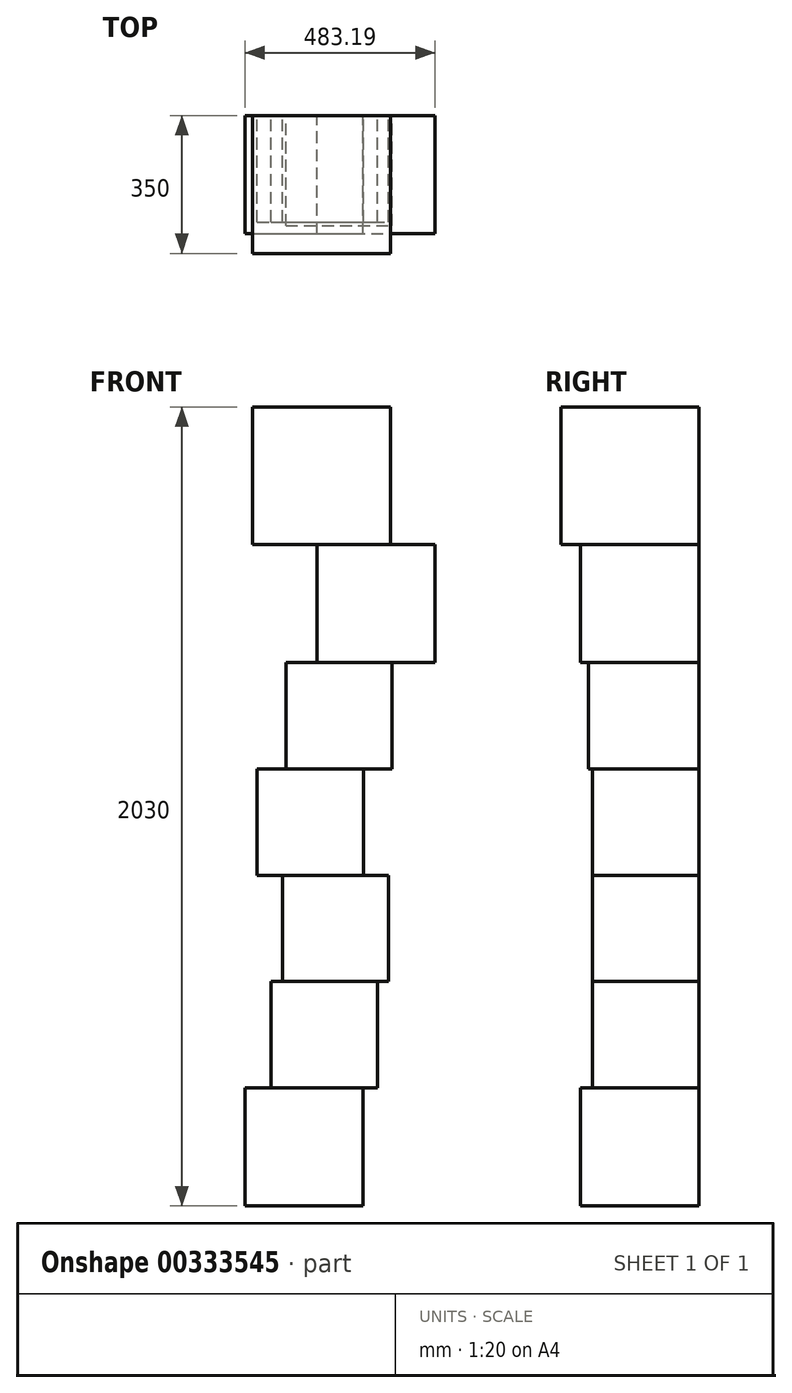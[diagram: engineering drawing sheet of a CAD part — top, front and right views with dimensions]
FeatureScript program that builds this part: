
annotation { "Feature Type Name" : "Feature", "Feature Type Description" : "" }
export const myFeature = defineFeature(function(context is Context, id is Id, definition is map)
    precondition{}
    {
        {
            assignVariable(context, id + "F0", {"name" : "a", "anyValue" : 270});
        }
        {
            assignVariable(context, id + "F1", {"name" : "b", "anyValue" : 350});
        }
        {
            assignVariable(context, id + "F2", {"name" : "c", "anyValue" : 300});
        }
        {
            var Q0;
            Q0=qCreatedBy(makeId("Front.planeOp"),FACE);
            var sketch = newSketch(context, id + "F3", { "sketchPlane" : qUnion([Q0])});
            skLineSegment(sketch, "E0.bottom", {"start": v(0, 0) * mm, "end": v(500, 0) * mm});
            skLineSegment(sketch, "E0.top", {"start": v(0, 60) * mm, "end": v(500, 60) * mm});
            skLineSegment(sketch, "E0.left", {"start": v(0, 0) * mm, "end": v(0, 60) * mm});
            skLineSegment(sketch, "E0.right", {"start": v(500, 0) * mm, "end": v(500, 60) * mm});
            skLineSegment(sketch, "E1", {"start": v(0, 0) * mm, "end": v(500, 0) * mm, "construction": true});
            skLineSegment(sketch, "E2", {"start": v(0, 0) * mm, "end": v(0, 60) * mm, "construction": true});
            skLineSegment(sketch, "E3.bottom", {"start": v(13.65, 60) * mm, "end": v(363.65, 60) * mm});
            skLineSegment(sketch, "E3.top", {"start": v(13.65, 410) * mm, "end": v(363.65, 410) * mm});
            skLineSegment(sketch, "E3.left", {"start": v(13.65, 60) * mm, "end": v(13.65, 410) * mm});
            skLineSegment(sketch, "E3.right", {"start": v(363.65, 60) * mm, "end": v(363.65, 410) * mm});
            skLineSegment(sketch, "E4.bottom", {"start": v(106.14, 410) * mm, "end": v(406.14, 410) * mm});
            skLineSegment(sketch, "E4.top", {"start": v(106.14, 710) * mm, "end": v(406.14, 710) * mm});
            skLineSegment(sketch, "E4.left", {"start": v(106.14, 410) * mm, "end": v(106.14, 710) * mm});
            skLineSegment(sketch, "E4.right", {"start": v(406.14, 410) * mm, "end": v(406.14, 710) * mm});
            skLineSegment(sketch, "E5.bottom", {"start": v(172.85, 710) * mm, "end": v(442.85, 710) * mm});
            skLineSegment(sketch, "E5.top", {"start": v(172.85, 980) * mm, "end": v(442.85, 980) * mm});
            skLineSegment(sketch, "E5.left", {"start": v(172.85, 710) * mm, "end": v(172.85, 980) * mm});
            skLineSegment(sketch, "E5.right", {"start": v(442.85, 710) * mm, "end": v(442.85, 980) * mm});
            skLineSegment(sketch, "E6.bottom", {"start": v(201.48, 980) * mm, "end": v(471.48, 980) * mm});
            skLineSegment(sketch, "E6.top", {"start": v(201.48, 1250) * mm, "end": v(471.48, 1250) * mm});
            skLineSegment(sketch, "E6.left", {"start": v(201.48, 980) * mm, "end": v(201.48, 1250) * mm});
            skLineSegment(sketch, "E6.right", {"start": v(471.48, 980) * mm, "end": v(471.48, 1250) * mm});
            skLineSegment(sketch, "E7.bottom", {"start": v(0, 0) * mm, "end": v(900, 0) * mm, "construction": true});
            skLineSegment(sketch, "E7.top", {"start": v(0, 1750) * mm, "end": v(900, 1750) * mm, "construction": true});
            skLineSegment(sketch, "E7.left", {"start": v(0, 0) * mm, "end": v(0, 1750) * mm, "construction": true});
            skLineSegment(sketch, "E7.right", {"start": v(900, 0) * mm, "end": v(900, 1750) * mm, "construction": true});
            skLineSegment(sketch, "E8", {"start": v(0, 900) * mm, "end": v(900, 900) * mm, "construction": true});
            skLineSegment(sketch, "E9.bottom", {"start": v(137.05, 1250) * mm, "end": v(407.05, 1250) * mm});
            skLineSegment(sketch, "E9.top", {"start": v(137.05, 1520) * mm, "end": v(407.05, 1520) * mm});
            skLineSegment(sketch, "E9.left", {"start": v(137.05, 1250) * mm, "end": v(137.05, 1520) * mm});
            skLineSegment(sketch, "E9.right", {"start": v(407.05, 1250) * mm, "end": v(407.05, 1520) * mm});
            skLineSegment(sketch, "E10.bottom", {"start": v(210.21, 1520) * mm, "end": v(480.21, 1520) * mm});
            skLineSegment(sketch, "E10.top", {"start": v(210.21, 1790) * mm, "end": v(480.21, 1790) * mm});
            skLineSegment(sketch, "E10.left", {"start": v(210.21, 1520) * mm, "end": v(210.21, 1790) * mm});
            skLineSegment(sketch, "E10.right", {"start": v(480.21, 1520) * mm, "end": v(480.21, 1790) * mm});
            skLineSegment(sketch, "E11", {"start": v(0, 1750) * mm, "end": v(0, 2550) * mm, "construction": true});
            skLineSegment(sketch, "E12", {"start": v(0, 2550) * mm, "end": v(900, 2550) * mm, "construction": true});
            skLineSegment(sketch, "E13", {"start": v(900, 1750) * mm, "end": v(900, 2550) * mm, "construction": true});
            skLineSegment(sketch, "E14.bottom", {"start": v(289.33, 1790) * mm, "end": v(589.33, 1790) * mm});
            skLineSegment(sketch, "E14.top", {"start": v(289.33, 2090) * mm, "end": v(589.33, 2090) * mm});
            skLineSegment(sketch, "E14.left", {"start": v(289.33, 1790) * mm, "end": v(289.33, 2090) * mm});
            skLineSegment(sketch, "E14.right", {"start": v(589.33, 1790) * mm, "end": v(589.33, 2090) * mm});
            skLineSegment(sketch, "E15.bottom", {"start": v(475.94, 2090) * mm, "end": v(125.94, 2090) * mm});
            skLineSegment(sketch, "E15.top", {"start": v(475.94, 2440) * mm, "end": v(125.94, 2440) * mm});
            skLineSegment(sketch, "E15.left", {"start": v(475.94, 2090) * mm, "end": v(475.94, 2440) * mm});
            skLineSegment(sketch, "E15.right", {"start": v(125.94, 2090) * mm, "end": v(125.94, 2440) * mm});
            skSolve(sketch);
        }
        {
            var Q0;
            Q0=makeQuery(id+"F3.imprint","IMPRINT",FACE,{"disambiguationData":[TD([[makeQuery(id+"F3.imprint","IMPRINT",EDGE,{"derivedFrom":sQuery(id+"F3.wireOp",EDGE,"E3.bottom")}),1.0]])]});
            var Q1;
            Q1=makeQuery(id+"F3.imprint","IMPRINT",FACE,{"disambiguationData":[TD([[makeQuery(id+"F3.imprint","IMPRINT",EDGE,{"derivedFrom":sQuery(id+"F3.wireOp",EDGE,"E15.top")}),1.0]])]});
            extrude(context, id + "F4", {"entities" : qUnion([Q0, Q1]), "depth" : getVariable(context, 'b') * mm});
        }
        {
            var Q0;
            {var subQ1=sQuery(id+"F3.wireOp",EDGE,"E4.top");Q0=makeQuery(id+"F3.imprint","IMPRINT",FACE,{"disambiguationData":[TD([[makeQuery(id+"F3.imprint","IMPRINT",EDGE,{"derivedFrom":subQ1}),-1.0]])]});}
            var Q1;
            {var subQ1=sQuery(id+"F3.wireOp",EDGE,"E14.top");Q1=makeQuery(id+"F3.imprint","IMPRINT",FACE,{"disambiguationData":[TD([[makeQuery(id+"F3.imprint","IMPRINT",EDGE,{"derivedFrom":subQ1}),-1.0]])]});}
            extrude(context, id + "F5", {"entities" : qUnion([Q0, Q1]), "depth" : getVariable(context, 'c') * mm});
        }
        {
            var Q0;
            {var subQ1=sQuery(id+"F3.wireOp",EDGE,"E5.top");Q0=makeQuery(id+"F3.imprint","IMPRINT",FACE,{"disambiguationData":[TD([[makeQuery(id+"F3.imprint","IMPRINT",EDGE,{"derivedFrom":subQ1}),-1.0]])]});}
            extrude(context, id + "F6", {"entities" : qUnion([Q0]), "depth" : getVariable(context, 'a') * mm});
        }
        {
            var Q0;
            Q0=makeQuery(id+"F3.imprint","IMPRINT",FACE,{"disambiguationData":[TD([[makeQuery(id+"F3.imprint","IMPRINT",EDGE,{"derivedFrom":sQuery(id+"F3.wireOp",EDGE,"E6.top")}),-1.0]])]});
            extrude(context, id + "F7", {"entities" : qUnion([Q0]), "depth" : getVariable(context, 'a') * mm});
        }
        {
            var Q0;
            Q0=makeQuery(id+"F3.imprint","IMPRINT",FACE,{"disambiguationData":[TD([[makeQuery(id+"F3.imprint","IMPRINT",EDGE,{"derivedFrom":sQuery(id+"F3.wireOp",EDGE,"E9.top")}),-1.0]])]});
            extrude(context, id + "F8", {"entities" : qUnion([Q0]), "depth" : getVariable(context, 'a') * mm});
        }
        {
            var Q0;
            Q0=makeQuery(id+"F3.imprint","IMPRINT",FACE,{"disambiguationData":[TD([[makeQuery(id+"F3.imprint","IMPRINT",EDGE,{"derivedFrom":sQuery(id+"F3.wireOp",EDGE,"E10.top")}),-1.0]])]});
            extrude(context, id + "F9", {"entities" : qUnion([Q0]), "depth" : 280 * mm});
        }
    });
